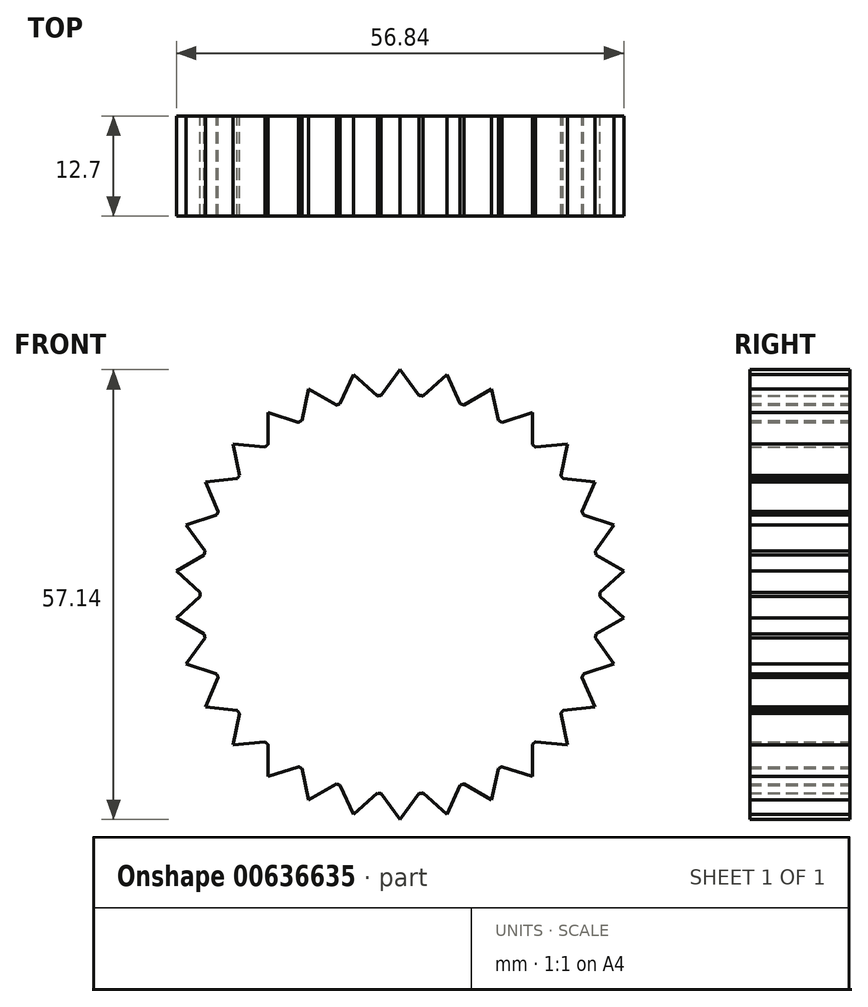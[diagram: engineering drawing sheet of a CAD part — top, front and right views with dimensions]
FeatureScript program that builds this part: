
annotation { "Feature Type Name" : "Feature", "Feature Type Description" : "" }
export const myFeature = defineFeature(function(context is Context, id is Id, definition is map)
    precondition{}
    {
        {
            var Q0;
            Q0=qCreatedBy(makeId("Front.planeOp"),FACE);
            var sketch = newSketch(context, id + "F0", { "sketchPlane" : qUnion([Q0])});
            skCircle(sketch, "E0", {"center": v(0, 0) * mm, "radius": 25.4 * mm});
            skLineSegment(sketch, "E1", {"start": v(0, 25.4) * mm, "end": v(0, 28.58) * mm, "construction": true});
            skLineSegment(sketch, "E2", {"start": v(0, 28.58) * mm, "end": v(-2.4, 25.29) * mm});
            skLineSegment(sketch, "E3.MirrorCS", {"start": v(0, 28.58) * mm, "end": v(2.4, 25.29) * mm});
            skLineSegment(sketch, "E4.1.0", {"start": v(-5.94, 27.95) * mm, "end": v(-7.61, 24.23) * mm});
            skLineSegment(sketch, "E4.1.1", {"start": v(-5.94, 27.95) * mm, "end": v(-2.9, 25.23) * mm});
            skLineSegment(sketch, "E4.2.0", {"start": v(-11.62, 26.1) * mm, "end": v(-12.48, 22.12) * mm});
            skLineSegment(sketch, "E4.2.1", {"start": v(-11.62, 26.1) * mm, "end": v(-8.09, 24.08) * mm});
            skLineSegment(sketch, "E4.3.0", {"start": v(-16.8, 23.12) * mm, "end": v(-16.81, 19.04) * mm});
            skLineSegment(sketch, "E4.3.1", {"start": v(-16.8, 23.12) * mm, "end": v(-12.91, 21.87) * mm});
            skLineSegment(sketch, "E4.4.0", {"start": v(-21.24, 19.12) * mm, "end": v(-20.4, 15.13) * mm});
            skLineSegment(sketch, "E4.4.1", {"start": v(-21.24, 19.12) * mm, "end": v(-17.18, 18.7) * mm});
            skLineSegment(sketch, "E4.5.0", {"start": v(-24.75, 14.29) * mm, "end": v(-23.1, 10.56) * mm});
            skLineSegment(sketch, "E4.5.1", {"start": v(-24.75, 14.29) * mm, "end": v(-20.7, 14.73) * mm});
            skLineSegment(sketch, "E4.6.0", {"start": v(-27.18, 8.83) * mm, "end": v(-24.8, 5.52) * mm});
            skLineSegment(sketch, "E4.6.1", {"start": v(-27.18, 8.83) * mm, "end": v(-23.3, 10.1) * mm});
            skLineSegment(sketch, "E4.7.0", {"start": v(-28.42, 2.99) * mm, "end": v(-25.4, 0.25) * mm});
            skLineSegment(sketch, "E4.7.1", {"start": v(-28.42, 2.99) * mm, "end": v(-24.9, 5.04) * mm});
            skLineSegment(sketch, "E4.8.0", {"start": v(-28.42, -2.99) * mm, "end": v(-24.9, -5.04) * mm});
            skLineSegment(sketch, "E4.8.1", {"start": v(-28.42, -2.99) * mm, "end": v(-25.4, -0.25) * mm});
            skLineSegment(sketch, "E4.9.0", {"start": v(-27.18, -8.83) * mm, "end": v(-23.3, -10.1) * mm});
            skLineSegment(sketch, "E4.9.1", {"start": v(-27.18, -8.83) * mm, "end": v(-24.8, -5.52) * mm});
            skLineSegment(sketch, "E4.10.0", {"start": v(-24.75, -14.29) * mm, "end": v(-20.7, -14.73) * mm});
            skLineSegment(sketch, "E4.10.1", {"start": v(-24.75, -14.29) * mm, "end": v(-23.1, -10.56) * mm});
            skLineSegment(sketch, "E4.11.0", {"start": v(-21.24, -19.12) * mm, "end": v(-17.18, -18.7) * mm});
            skLineSegment(sketch, "E4.11.1", {"start": v(-21.24, -19.12) * mm, "end": v(-20.4, -15.13) * mm});
            skLineSegment(sketch, "E4.12.0", {"start": v(-16.8, -23.12) * mm, "end": v(-12.91, -21.87) * mm});
            skLineSegment(sketch, "E4.12.1", {"start": v(-16.8, -23.12) * mm, "end": v(-16.81, -19.04) * mm});
            skLineSegment(sketch, "E4.13.0", {"start": v(-11.62, -26.1) * mm, "end": v(-8.09, -24.08) * mm});
            skLineSegment(sketch, "E4.13.1", {"start": v(-11.62, -26.1) * mm, "end": v(-12.48, -22.12) * mm});
            skLineSegment(sketch, "E4.14.0", {"start": v(-5.94, -27.95) * mm, "end": v(-2.9, -25.23) * mm});
            skLineSegment(sketch, "E4.14.1", {"start": v(-5.94, -27.95) * mm, "end": v(-7.61, -24.23) * mm});
            skLineSegment(sketch, "E4.15.0", {"start": v(0, -28.58) * mm, "end": v(2.4, -25.29) * mm});
            skLineSegment(sketch, "E4.15.1", {"start": v(0, -28.58) * mm, "end": v(-2.4, -25.29) * mm});
            skLineSegment(sketch, "E4.16.0", {"start": v(5.94, -27.95) * mm, "end": v(7.61, -24.23) * mm});
            skLineSegment(sketch, "E4.16.1", {"start": v(5.94, -27.95) * mm, "end": v(2.9, -25.23) * mm});
            skLineSegment(sketch, "E4.17.0", {"start": v(11.62, -26.1) * mm, "end": v(12.48, -22.12) * mm});
            skLineSegment(sketch, "E4.17.1", {"start": v(11.62, -26.1) * mm, "end": v(8.09, -24.08) * mm});
            skLineSegment(sketch, "E4.18.0", {"start": v(16.8, -23.12) * mm, "end": v(16.81, -19.04) * mm});
            skLineSegment(sketch, "E4.18.1", {"start": v(16.8, -23.12) * mm, "end": v(12.91, -21.87) * mm});
            skLineSegment(sketch, "E4.19.0", {"start": v(21.24, -19.12) * mm, "end": v(20.4, -15.13) * mm});
            skLineSegment(sketch, "E4.19.1", {"start": v(21.24, -19.12) * mm, "end": v(17.18, -18.7) * mm});
            skLineSegment(sketch, "E4.20.0", {"start": v(24.75, -14.29) * mm, "end": v(23.1, -10.56) * mm});
            skLineSegment(sketch, "E4.20.1", {"start": v(24.75, -14.29) * mm, "end": v(20.7, -14.73) * mm});
            skLineSegment(sketch, "E4.21.0", {"start": v(27.18, -8.83) * mm, "end": v(24.8, -5.52) * mm});
            skLineSegment(sketch, "E4.21.1", {"start": v(27.18, -8.83) * mm, "end": v(23.3, -10.1) * mm});
            skLineSegment(sketch, "E4.22.0", {"start": v(28.42, -2.99) * mm, "end": v(25.4, -0.25) * mm});
            skLineSegment(sketch, "E4.22.1", {"start": v(28.42, -2.99) * mm, "end": v(24.9, -5.04) * mm});
            skLineSegment(sketch, "E4.23.0", {"start": v(28.42, 2.99) * mm, "end": v(24.9, 5.04) * mm});
            skLineSegment(sketch, "E4.23.1", {"start": v(28.42, 2.99) * mm, "end": v(25.4, 0.25) * mm});
            skLineSegment(sketch, "E4.24.0", {"start": v(27.18, 8.83) * mm, "end": v(23.3, 10.1) * mm});
            skLineSegment(sketch, "E4.24.1", {"start": v(27.18, 8.83) * mm, "end": v(24.8, 5.52) * mm});
            skLineSegment(sketch, "E4.25.0", {"start": v(24.75, 14.29) * mm, "end": v(20.7, 14.73) * mm});
            skLineSegment(sketch, "E4.25.1", {"start": v(24.75, 14.29) * mm, "end": v(23.1, 10.56) * mm});
            skLineSegment(sketch, "E4.26.0", {"start": v(21.24, 19.12) * mm, "end": v(17.18, 18.7) * mm});
            skLineSegment(sketch, "E4.26.1", {"start": v(21.24, 19.12) * mm, "end": v(20.4, 15.13) * mm});
            skLineSegment(sketch, "E4.27.0", {"start": v(16.8, 23.12) * mm, "end": v(12.91, 21.87) * mm});
            skLineSegment(sketch, "E4.27.1", {"start": v(16.8, 23.12) * mm, "end": v(16.81, 19.04) * mm});
            skLineSegment(sketch, "E4.28.0", {"start": v(11.62, 26.1) * mm, "end": v(8.09, 24.08) * mm});
            skLineSegment(sketch, "E4.28.1", {"start": v(11.62, 26.1) * mm, "end": v(12.48, 22.12) * mm});
            skLineSegment(sketch, "E4.29.0", {"start": v(5.94, 27.95) * mm, "end": v(2.9, 25.23) * mm});
            skLineSegment(sketch, "E4.29.1", {"start": v(5.94, 27.95) * mm, "end": v(7.61, 24.23) * mm});
            skSolve(sketch);
        }
        {
            var Q0;
            {var subQ0=sQuery(id+"F0.wireOp",EDGE,"E0");var subQ33=makeQuery(id+"F0.imprint","INTERSECT",VERTEX,{"derivedFrom":[subQ0,sQuery(id+"F0.wireOp",EDGE,"E4.23.0")]});Q0=makeQuery(id+"F0.imprint","IMPRINT",FACE,{"disambiguationData":[TD([[makeQuery(id+"F0.imprint","IMPRINT",EDGE,{"disambiguationData":[TD([[subQ33,1.0]])],"derivedFrom":subQ0}),1.0]])]});}
            var Q1;
            {var subQ0=sQuery(id+"F0.wireOp",EDGE,"E4.8.0");Q1=makeQuery(id+"F0.imprint","IMPRINT",FACE,{"disambiguationData":[TD([[makeQuery(id+"F0.imprint","IMPRINT",EDGE,{"derivedFrom":subQ0}),1.0]])]});}
            var Q2;
            {var subQ0=sQuery(id+"F0.wireOp",EDGE,"E4.7.0");Q2=makeQuery(id+"F0.imprint","IMPRINT",FACE,{"disambiguationData":[TD([[makeQuery(id+"F0.imprint","IMPRINT",EDGE,{"derivedFrom":subQ0}),1.0]])]});}
            var Q3;
            {var subQ0=sQuery(id+"F0.wireOp",EDGE,"E4.6.0");Q3=makeQuery(id+"F0.imprint","IMPRINT",FACE,{"disambiguationData":[TD([[makeQuery(id+"F0.imprint","IMPRINT",EDGE,{"derivedFrom":subQ0}),1.0]])]});}
            var Q4;
            {var subQ0=sQuery(id+"F0.wireOp",EDGE,"E4.5.0");Q4=makeQuery(id+"F0.imprint","IMPRINT",FACE,{"disambiguationData":[TD([[makeQuery(id+"F0.imprint","IMPRINT",EDGE,{"derivedFrom":subQ0}),1.0]])]});}
            var Q5;
            {var subQ0=sQuery(id+"F0.wireOp",EDGE,"E4.4.0");Q5=makeQuery(id+"F0.imprint","IMPRINT",FACE,{"disambiguationData":[TD([[makeQuery(id+"F0.imprint","IMPRINT",EDGE,{"derivedFrom":subQ0}),1.0]])]});}
            var Q6;
            {var subQ0=sQuery(id+"F0.wireOp",EDGE,"E4.3.0");Q6=makeQuery(id+"F0.imprint","IMPRINT",FACE,{"disambiguationData":[TD([[makeQuery(id+"F0.imprint","IMPRINT",EDGE,{"derivedFrom":subQ0}),1.0]])]});}
            var Q7;
            {var subQ0=sQuery(id+"F0.wireOp",EDGE,"E4.2.0");Q7=makeQuery(id+"F0.imprint","IMPRINT",FACE,{"disambiguationData":[TD([[makeQuery(id+"F0.imprint","IMPRINT",EDGE,{"derivedFrom":subQ0}),1.0]])]});}
            var Q8;
            {var subQ0=sQuery(id+"F0.wireOp",EDGE,"E4.1.0");Q8=makeQuery(id+"F0.imprint","IMPRINT",FACE,{"disambiguationData":[TD([[makeQuery(id+"F0.imprint","IMPRINT",EDGE,{"derivedFrom":subQ0}),1.0]])]});}
            var Q9;
            {var subQ0=sQuery(id+"F0.wireOp",EDGE,"E2");Q9=makeQuery(id+"F0.imprint","IMPRINT",FACE,{"disambiguationData":[TD([[makeQuery(id+"F0.imprint","IMPRINT",EDGE,{"derivedFrom":subQ0}),1.0]])]});}
            var Q10;
            {var subQ0=sQuery(id+"F0.wireOp",EDGE,"E4.29.0");Q10=makeQuery(id+"F0.imprint","IMPRINT",FACE,{"disambiguationData":[TD([[makeQuery(id+"F0.imprint","IMPRINT",EDGE,{"derivedFrom":subQ0}),1.0]])]});}
            var Q11;
            {var subQ0=sQuery(id+"F0.wireOp",EDGE,"E4.27.0");Q11=makeQuery(id+"F0.imprint","IMPRINT",FACE,{"disambiguationData":[TD([[makeQuery(id+"F0.imprint","IMPRINT",EDGE,{"derivedFrom":subQ0}),1.0]])]});}
            var Q12;
            {var subQ0=sQuery(id+"F0.wireOp",EDGE,"E4.26.0");Q12=makeQuery(id+"F0.imprint","IMPRINT",FACE,{"disambiguationData":[TD([[makeQuery(id+"F0.imprint","IMPRINT",EDGE,{"derivedFrom":subQ0}),1.0]])]});}
            var Q13;
            {var subQ0=sQuery(id+"F0.wireOp",EDGE,"E4.25.0");Q13=makeQuery(id+"F0.imprint","IMPRINT",FACE,{"disambiguationData":[TD([[makeQuery(id+"F0.imprint","IMPRINT",EDGE,{"derivedFrom":subQ0}),1.0]])]});}
            var Q14;
            {var subQ0=sQuery(id+"F0.wireOp",EDGE,"E4.24.0");Q14=makeQuery(id+"F0.imprint","IMPRINT",FACE,{"disambiguationData":[TD([[makeQuery(id+"F0.imprint","IMPRINT",EDGE,{"derivedFrom":subQ0}),1.0]])]});}
            var Q15;
            {var subQ0=sQuery(id+"F0.wireOp",EDGE,"E4.28.0");Q15=makeQuery(id+"F0.imprint","IMPRINT",FACE,{"disambiguationData":[TD([[makeQuery(id+"F0.imprint","IMPRINT",EDGE,{"derivedFrom":subQ0}),1.0]])]});}
            var Q16;
            {var subQ0=sQuery(id+"F0.wireOp",EDGE,"E4.23.0");Q16=makeQuery(id+"F0.imprint","IMPRINT",FACE,{"disambiguationData":[TD([[makeQuery(id+"F0.imprint","IMPRINT",EDGE,{"derivedFrom":subQ0}),1.0]])]});}
            var Q17;
            {var subQ0=sQuery(id+"F0.wireOp",EDGE,"E4.22.0");Q17=makeQuery(id+"F0.imprint","IMPRINT",FACE,{"disambiguationData":[TD([[makeQuery(id+"F0.imprint","IMPRINT",EDGE,{"derivedFrom":subQ0}),1.0]])]});}
            var Q18;
            {var subQ0=sQuery(id+"F0.wireOp",EDGE,"E4.21.0");Q18=makeQuery(id+"F0.imprint","IMPRINT",FACE,{"disambiguationData":[TD([[makeQuery(id+"F0.imprint","IMPRINT",EDGE,{"derivedFrom":subQ0}),1.0]])]});}
            var Q19;
            {var subQ0=sQuery(id+"F0.wireOp",EDGE,"E4.20.0");Q19=makeQuery(id+"F0.imprint","IMPRINT",FACE,{"disambiguationData":[TD([[makeQuery(id+"F0.imprint","IMPRINT",EDGE,{"derivedFrom":subQ0}),1.0]])]});}
            var Q20;
            {var subQ0=sQuery(id+"F0.wireOp",EDGE,"E4.19.0");Q20=makeQuery(id+"F0.imprint","IMPRINT",FACE,{"disambiguationData":[TD([[makeQuery(id+"F0.imprint","IMPRINT",EDGE,{"derivedFrom":subQ0}),1.0]])]});}
            var Q21;
            {var subQ0=sQuery(id+"F0.wireOp",EDGE,"E4.17.0");Q21=makeQuery(id+"F0.imprint","IMPRINT",FACE,{"disambiguationData":[TD([[makeQuery(id+"F0.imprint","IMPRINT",EDGE,{"derivedFrom":subQ0}),1.0]])]});}
            var Q22;
            {var subQ0=sQuery(id+"F0.wireOp",EDGE,"E4.16.0");Q22=makeQuery(id+"F0.imprint","IMPRINT",FACE,{"disambiguationData":[TD([[makeQuery(id+"F0.imprint","IMPRINT",EDGE,{"derivedFrom":subQ0}),1.0]])]});}
            var Q23;
            {var subQ0=sQuery(id+"F0.wireOp",EDGE,"E4.15.0");Q23=makeQuery(id+"F0.imprint","IMPRINT",FACE,{"disambiguationData":[TD([[makeQuery(id+"F0.imprint","IMPRINT",EDGE,{"derivedFrom":subQ0}),1.0]])]});}
            var Q24;
            {var subQ0=sQuery(id+"F0.wireOp",EDGE,"E4.14.0");Q24=makeQuery(id+"F0.imprint","IMPRINT",FACE,{"disambiguationData":[TD([[makeQuery(id+"F0.imprint","IMPRINT",EDGE,{"derivedFrom":subQ0}),1.0]])]});}
            var Q25;
            {var subQ0=sQuery(id+"F0.wireOp",EDGE,"E4.13.0");Q25=makeQuery(id+"F0.imprint","IMPRINT",FACE,{"disambiguationData":[TD([[makeQuery(id+"F0.imprint","IMPRINT",EDGE,{"derivedFrom":subQ0}),1.0]])]});}
            var Q26;
            {var subQ0=sQuery(id+"F0.wireOp",EDGE,"E4.12.0");Q26=makeQuery(id+"F0.imprint","IMPRINT",FACE,{"disambiguationData":[TD([[makeQuery(id+"F0.imprint","IMPRINT",EDGE,{"derivedFrom":subQ0}),1.0]])]});}
            var Q27;
            {var subQ0=sQuery(id+"F0.wireOp",EDGE,"E4.11.0");Q27=makeQuery(id+"F0.imprint","IMPRINT",FACE,{"disambiguationData":[TD([[makeQuery(id+"F0.imprint","IMPRINT",EDGE,{"derivedFrom":subQ0}),1.0]])]});}
            var Q28;
            {var subQ0=sQuery(id+"F0.wireOp",EDGE,"E4.10.0");Q28=makeQuery(id+"F0.imprint","IMPRINT",FACE,{"disambiguationData":[TD([[makeQuery(id+"F0.imprint","IMPRINT",EDGE,{"derivedFrom":subQ0}),1.0]])]});}
            var Q29;
            {var subQ0=sQuery(id+"F0.wireOp",EDGE,"E4.9.0");Q29=makeQuery(id+"F0.imprint","IMPRINT",FACE,{"disambiguationData":[TD([[makeQuery(id+"F0.imprint","IMPRINT",EDGE,{"derivedFrom":subQ0}),1.0]])]});}
            var Q30;
            {var subQ0=sQuery(id+"F0.wireOp",EDGE,"E4.18.0");Q30=makeQuery(id+"F0.imprint","IMPRINT",FACE,{"disambiguationData":[TD([[makeQuery(id+"F0.imprint","IMPRINT",EDGE,{"derivedFrom":subQ0}),1.0]])]});}
            extrude(context, id + "F1", {"entities" : qUnion([Q0, Q1, Q2, Q3, Q4, Q5, Q6, Q7, Q8, Q9, Q10, Q11, Q12, Q13, Q14, Q15, Q16, Q17, Q18, Q19, Q20, Q21, Q22, Q23, Q24, Q25, Q26, Q27, Q28, Q29, Q30]), "depth" : 12.7 * mm, "offsetDistance" : 25.4 * mm});
        }
    });
